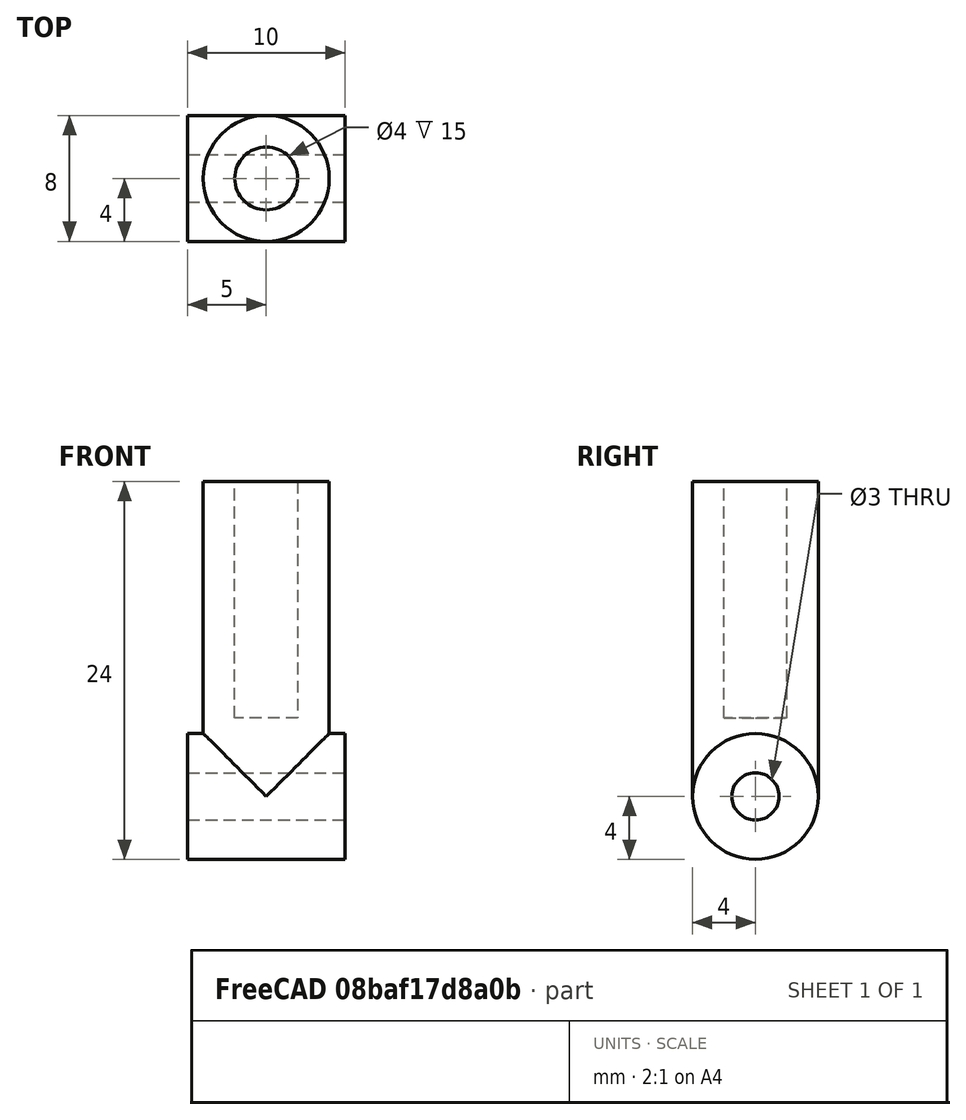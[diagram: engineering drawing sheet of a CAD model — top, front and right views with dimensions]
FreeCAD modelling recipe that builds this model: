
FCSTD DOCUMENT  (FreeCAD 0.20R29177 +426 (Git))
Label: damper-cylinder
License: All rights reserved
LicenseURL: http://en.wikipedia.org/wiki/All_rights_reserved
objects: TechDraw::DrawViewDimension×7, Sketcher::SketchObject×4, PartDesign::Plane×3, TechDraw::DrawProjGroupItem×3, PartDesign::Pocket×2, PartDesign::Revolution×1, PartDesign::Pad×1, PartDesign::Body×1, TechDraw::DrawSVGTemplate×1, TechDraw::DrawProjGroup×1, TechDraw::DrawPage×1
note: 16 computed .brp shape members not serialized (recipe doc carries the construction recipe); baked Part::Feature solids carry a one-line shape summary decoded from their .brp

FEATURE [PartDesign::Plane] DatumPlane
  Length = 60
  MapMode = 5
  Placement = pos=(0,0,0) rot=(1,0,0;1.5708rad)
  ResizeMode = 0
  Support = -> [XZ_Plane]
  Width = 60
FEATURE [Sketcher::SketchObject] Sketch
  FullyConstrained = true
  MapMode = 5
  Placement = pos=(0,0,0) rot=(1,0,0;1.5708rad)
  Support = -> [DatumPlane]
  sketch-geometry (4):
    g0: LineSegment StartX=0 StartY=0 StartZ=0 EndX=4 EndY=0 EndZ=0
    g1: LineSegment StartX=4 StartY=0 StartZ=0 EndX=4 EndY=20 EndZ=0
    g2: LineSegment StartX=4 StartY=20 StartZ=0 EndX=0 EndY=20 EndZ=0
    g3: LineSegment StartX=0 StartY=20 StartZ=0 EndX=0 EndY=0 EndZ=0
  constraints (11):
    c: Coincident(g0,g1)
    c: Coincident(g1,g2)
    c: Coincident(g2,g3)
    c: Coincident(g3,g0)
    c: Horizontal(g0)
    c: Horizontal(g2)
    c: Vertical(g1)
    c: Vertical(g3)
    c: Coincident(g0,g-1)
    c: DistanceX(g2,g2) = 4
    c: DistanceY(g1,g1) = 20
FEATURE [PartDesign::Revolution] Revolution
  Angle = 360
  Axis = (0,2e-16,1)
  Base = (0,0,0)
  Placement = pos=(0,0,0) rot=(1,0,0;1.5708rad)
  Profile = -> Sketch
  ReferenceAxis = -> Sketch [V_Axis]
  Reversed = true
FEATURE [PartDesign::Plane] DatumPlane001
  Length = 60
  MapMode = 5
  Placement = pos=(0,0,0) rot=(0.57735,0.57735,0.57735;2.0944rad)
  ResizeMode = 0
  Support = -> [YZ_Plane]
  Width = 60
FEATURE [Sketcher::SketchObject] Sketch001
  FullyConstrained = true
  MapMode = 5
  Placement = pos=(0,0,0) rot=(0.57735,0.57735,0.57735;2.0944rad)
  Support = -> [DatumPlane001]
  sketch-geometry (1):
    g0: Circle CenterX=0 CenterY=0 CenterZ=0 NormalX=0 NormalY=0 NormalZ=1 AngleXU=0 Radius=4
  constraints (2):
    c: Radius(g0) = 4
    c: Coincident(g0,g-1)
FEATURE [PartDesign::Pad] Pad
  BaseFeature = -> Revolution
  Direction = (1,1,1)
  Length = 10
  Length2 = 100
  Midplane = true
  Placement = pos=(0,0,0) rot=(1,0,0;1.5708rad)
  Profile = -> Sketch001
  Type = 0
FEATURE [Sketcher::SketchObject] Sketch002
  FullyConstrained = true
  MapMode = 5
  Placement = pos=(0,0,0) rot=(0.57735,0.57735,0.57735;2.0944rad)
  Support = -> [DatumPlane001]
  sketch-geometry (1):
    g0: Circle CenterX=0 CenterY=0 CenterZ=0 NormalX=0 NormalY=0 NormalZ=1 AngleXU=0 Radius=1.5
  constraints (2):
    c: Coincident(g0,g-1)
    c: Radius(g0) = 1.5
FEATURE [PartDesign::Pocket] Pocket
  BaseFeature = -> Pad
  Direction = (1,1,1)
  Length = 5
  Length2 = 100
  Midplane = true
  Placement = pos=(0,0,0) rot=(1,0,0;1.5708rad)
  Profile = -> Sketch002
  Type = 1
FEATURE [PartDesign::Plane] DatumPlane002
  AttachmentOffset = pos=(0,0,20) rot=(0,0,1;0rad)
  Length = 60
  MapMode = 5
  Placement = pos=(0,0,20) rot=(0,0,1;0rad)
  ResizeMode = 0
  Support = -> [XY_Plane]
  Width = 60
FEATURE [Sketcher::SketchObject] Sketch003
  FullyConstrained = true
  MapMode = 5
  Placement = pos=(0,0,20) rot=(0,0,1;0rad)
  Support = -> [DatumPlane002]
  sketch-geometry (1):
    g0: Circle CenterX=0 CenterY=0 CenterZ=0 NormalX=0 NormalY=0 NormalZ=1 AngleXU=0 Radius=2
  constraints (2):
    c: Coincident(g0,g-1)
    c: Radius(g0) = 2
FEATURE [PartDesign::Pocket] Pocket001
  BaseFeature = -> Pocket
  Direction = (1,1,1)
  Length = 15
  Length2 = 100
  Placement = pos=(0,0,0) rot=(1,0,0;1.5708rad)
  Profile = -> Sketch003
  Type = 0
FEATURE [PartDesign::Body] Body
  Group = -> [DatumPlane,Sketch,Revolution,DatumPlane001,Sketch001,Pad,Sketch002,Pocket,DatumPlane002,Sketch003,Pocket001]
  Origin = -> Origin
  Tip = -> Pocket001
FEATURE [TechDraw::DrawSVGTemplate] Template
  EditableTexts = Designed_by_Name=Aleksander Sadowski; FC-SC=4:1; FC-Title=Dämpfer-Feder Zylinder; Subtitle=Mars Rover
  Height = 210
  Orientation = 1
  Width = 297
FEATURE [TechDraw::DrawProjGroupItem] ProjItem  label="Front"
  CoarseView = false
  Direction = (1,0,0)
  Focus = 100
  HardHidden = false
  IsoCount = 0
  IsoHidden = false
  IsoVisible = false
  LockPosition = true
  Perspective = false
  Rotation = 0
  RotationVector = (0,1,0)
  Scale = 4
  ScaleType = 2
  SeamHidden = false
  SeamVisible = true
  SmoothHidden = false
  SmoothVisible = true
  Source = -> [Body]
  Type = 0
  X = 0
  XDirection = (0,1,0)
  Y = 0
FEATURE [TechDraw::DrawProjGroupItem] ProjItem002  label="FrontTopLeft"
  CoarseView = false
  Direction = (0.57735,-0.57735,0.57735)
  Focus = 100
  HardHidden = false
  IsoCount = 0
  IsoHidden = false
  IsoVisible = false
  LockPosition = false
  Perspective = false
  Rotation = 0
  RotationVector = (1,0,0)
  Scale = 4
  ScaleType = 2
  SeamHidden = false
  SeamVisible = true
  SmoothHidden = false
  SmoothVisible = true
  Source = -> [Body]
  Type = 6
  X = 112.328
  XDirection = (0.707107,0.707107,0)
  Y = -112.328
FEATURE [TechDraw::DrawProjGroupItem] ProjItem003  label="Top"
  CoarseView = false
  Direction = (0,0,1)
  Focus = 100
  HardHidden = false
  IsoCount = 0
  IsoHidden = false
  IsoVisible = false
  LockPosition = false
  Perspective = false
  Rotation = 0
  RotationVector = (1,0,0)
  Scale = 4
  ScaleType = 2
  SeamHidden = false
  SeamVisible = true
  SmoothHidden = false
  SmoothVisible = true
  Source = -> [Body]
  Type = 4
  X = 0
  XDirection = (0,1,0)
  Y = -112.328
FEATURE [TechDraw::DrawProjGroup] ProjGroup
  Anchor = -> ProjItem
  AutoDistribute = true
  LockPosition = false
  ProjectionType = 0
  Rotation = 0
  Scale = 4
  ScaleType = 2
  Source = -> [Body]
  Views = -> [ProjItem,ProjItem002,ProjItem003]
  X = 62.0791
  Y = 132.09
  spacingX = 15
  spacingY = 15
FEATURE [TechDraw::DrawViewDimension] Dimension
  AngleOverride = false
  Arbitrary = false
  ArbitraryTolerances = false
  EqualTolerance = true
  ExtensionAngle = 0
  FormatSpec = ⌀ %.0f
  FormatSpecOverTolerance = %+.2f
  FormatSpecUnderTolerance = %+.2f
  Inverted = false
  LineAngle = 0
  LockPosition = false
  MeasureType = 1
  OverTolerance = 0
  References2D = -> [ProjItem003]
  Rotation = 0
  ScaleType = 0
  TheoreticalExact = false
  Type = 5
  UnderTolerance = 0
  X = 23.2563
  Y = 12.8843
FEATURE [TechDraw::DrawViewDimension] Dimension001
  AngleOverride = false
  Arbitrary = false
  ArbitraryTolerances = false
  EqualTolerance = true
  ExtensionAngle = 0
  FormatSpec = ⌀ %.0f
  FormatSpecOverTolerance = %+.2f
  FormatSpecUnderTolerance = %+.2f
  Inverted = false
  LineAngle = 0
  LockPosition = false
  MeasureType = 1
  OverTolerance = 0
  References2D = -> [ProjItem]
  Rotation = 0
  ScaleType = 0
  TheoreticalExact = false
  Type = 5
  UnderTolerance = 0
  X = 24.8264
  Y = -37.2396
FEATURE [TechDraw::DrawViewDimension] Dimension002
  AngleOverride = false
  Arbitrary = false
  ArbitraryTolerances = false
  EqualTolerance = true
  ExtensionAngle = 0
  FormatSpec = ⌀ %.0f
  FormatSpecOverTolerance = %+.2f
  FormatSpecUnderTolerance = %+.2f
  Inverted = false
  LineAngle = 0
  LockPosition = false
  MeasureType = 1
  OverTolerance = 0
  References2D = -> [ProjItem]
  Rotation = 0
  ScaleType = 0
  TheoreticalExact = false
  Type = 5
  UnderTolerance = 0
  X = 20.2389
  Y = -51.002
FEATURE [TechDraw::DrawViewDimension] Dimension003
  AngleOverride = false
  Arbitrary = false
  ArbitraryTolerances = false
  EqualTolerance = true
  ExtensionAngle = 0
  FormatSpec = ⌀ %.0f
  FormatSpecOverTolerance = %+.2f
  FormatSpecUnderTolerance = %+.2f
  Inverted = false
  LineAngle = 0
  LockPosition = false
  MeasureType = 1
  OverTolerance = 0
  References2D = -> [ProjItem]
  Rotation = 0
  ScaleType = 0
  TheoreticalExact = false
  Type = 1
  UnderTolerance = 0
  X = 1.18243
  Y = 60.1199
FEATURE [TechDraw::DrawViewDimension] Dimension004
  AngleOverride = false
  Arbitrary = false
  ArbitraryTolerances = false
  EqualTolerance = true
  ExtensionAngle = 0
  FormatSpec = %.0f
  FormatSpecOverTolerance = %+.2f
  FormatSpecUnderTolerance = %+.2f
  Inverted = false
  LineAngle = 0
  LockPosition = false
  MeasureType = 1
  OverTolerance = 0
  References2D = -> [ProjItem]
  Rotation = 0
  ScaleType = 0
  TheoreticalExact = false
  Type = 2
  UnderTolerance = 0
  X = 27.8243
  Y = 9.77365
FEATURE [TechDraw::DrawViewDimension] Dimension005
  AngleOverride = false
  Arbitrary = false
  ArbitraryTolerances = false
  EqualTolerance = true
  ExtensionAngle = 0
  FormatSpec = %.2f
  FormatSpecOverTolerance = %+.2f
  FormatSpecUnderTolerance = %+.2f
  Inverted = false
  LineAngle = 0
  LockPosition = false
  MeasureType = 1
  OverTolerance = 0
  Rotation = 0
  ScaleType = 0
  TheoreticalExact = false
  Type = 1
  UnderTolerance = 0
  X = 3.6e-15
  Y = -48
FEATURE [TechDraw::DrawViewDimension] Dimension006
  AngleOverride = false
  Arbitrary = false
  ArbitraryTolerances = false
  EqualTolerance = true
  ExtensionAngle = 0
  FormatSpec = %.0f
  FormatSpecOverTolerance = %+.2f
  FormatSpecUnderTolerance = %+.2f
  Inverted = false
  LineAngle = 0
  LockPosition = false
  MeasureType = 1
  OverTolerance = 0
  References2D = -> [ProjItem003]
  Rotation = 0
  ScaleType = 0
  TheoreticalExact = false
  Type = 2
  UnderTolerance = 0
  X = 29.4051
  Y = 0.215565
FEATURE [TechDraw::DrawPage] Page
  KeepUpdated = true
  NextBalloonIndex = 1
  ProjectionType = 0
  Template = -> Template
  Views = -> [ProjGroup,Dimension,Dimension001,Dimension002,Dimension003,Dimension004,Dimension005,Dimension006]
